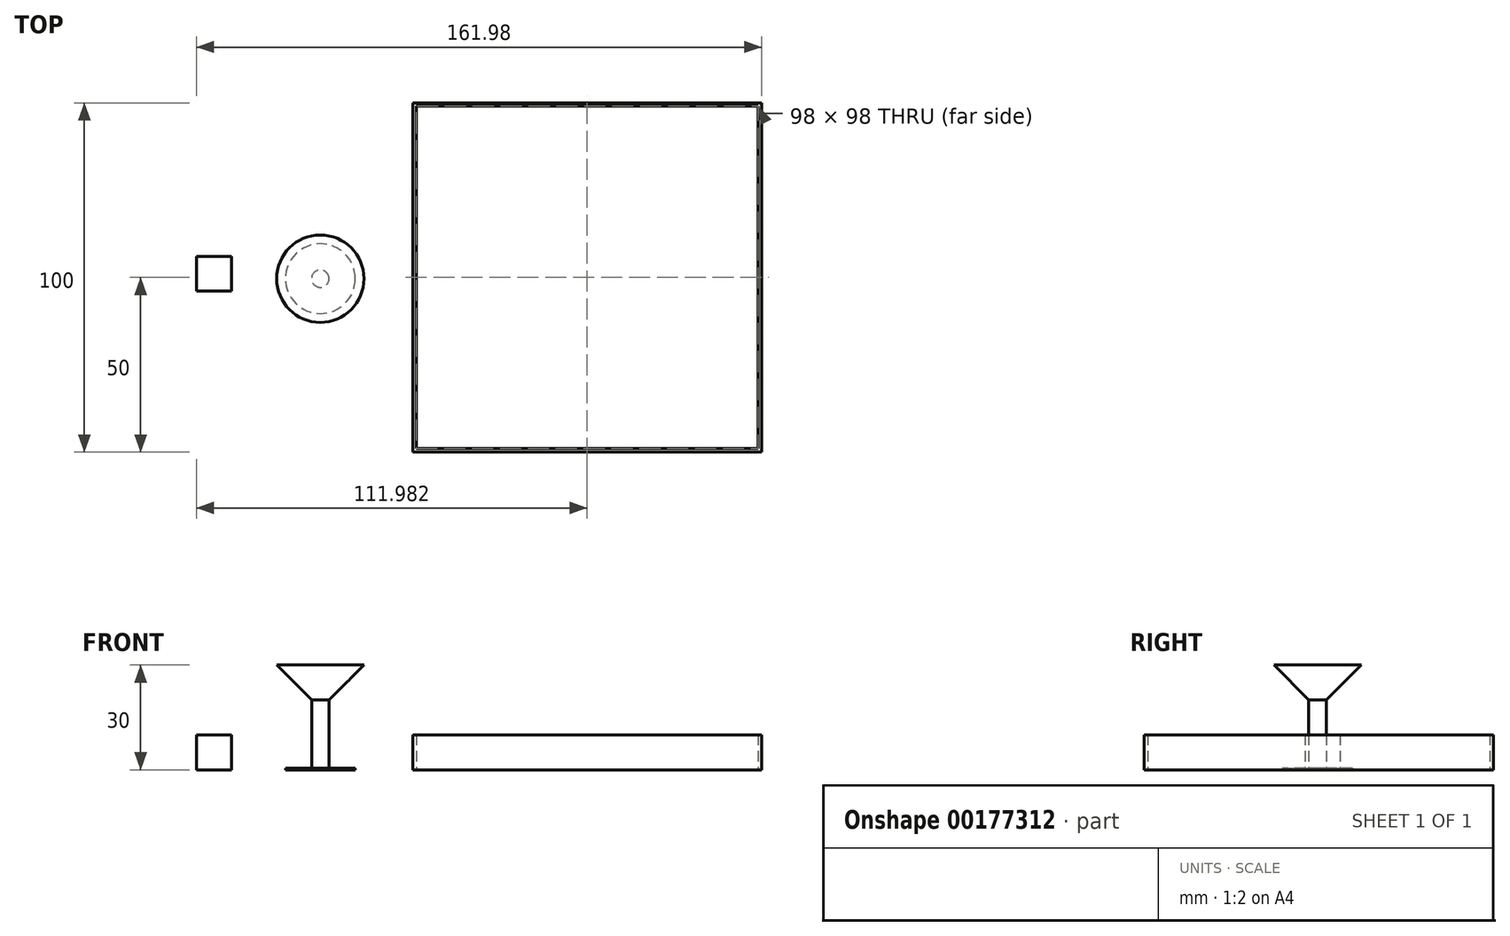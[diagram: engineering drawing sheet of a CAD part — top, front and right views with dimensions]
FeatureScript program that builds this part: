
annotation { "Feature Type Name" : "Feature", "Feature Type Description" : "" }
export const myFeature = defineFeature(function(context is Context, id is Id, definition is map)
    precondition{}
    {
        {
            var Q0;
            Q0=qCreatedBy(makeId("Top.planeOp"),FACE);
            var sketch = newSketch(context, id + "F0", { "sketchPlane" : qUnion([Q0])});
            skCircle(sketch, "E0", {"center": v(0, 0) * mm, "radius": 10 * mm});
            skCircle(sketch, "E1", {"center": v(0, 0) * mm, "radius": 2.5 * mm});
            skSolve(sketch);
        }
        {
            var Q0;
            Q0=makeQuery(id+"F0.imprint","IMPRINT",FACE,{"disambiguationData":[TD([[makeQuery(id+"F0.imprint","IMPRINT",EDGE,{"derivedFrom":sQuery(id+"F0.wireOp",EDGE,"E0")}),1.0]])]});
            extrude(context, id + "F1", {"entities" : qUnion([Q0]), "depth" : 0.4 * mm});
        }
        {
            var Q0;
            Q0=makeQuery(id+"F0.imprint","IMPRINT",FACE,{"disambiguationData":[TD([[makeQuery(id+"F0.imprint","IMPRINT",EDGE,{"derivedFrom":sQuery(id+"F0.wireOp",EDGE,"E1")}),1.0]])]});
            extrude(context, id + "F2", {"entities" : qUnion([Q0]), "operationType" : NewBodyOperationType.ADD, "depth" : 20 * mm});
        }
        {
            var Q0;
            Q0=makeQuery(id+"F2.opExtrude","CAP_FACE",FACE,{"disambiguationData":[OSD([sQuery(id+"F0.wireOp",EDGE,"E1")])],"isStart":false});
            extrude(context, id + "F3", {"entities" : qUnion([Q0]), "operationType" : NewBodyOperationType.ADD, "depth" : 10 * mm, "hasDraft" : true, "draftAngle" : 45 * degree});
        }
        {
            var Q0;
            Q0=qCreatedBy(makeId("Top.planeOp"),FACE);
            var sketch = newSketch(context, id + "F4", { "sketchPlane" : qUnion([Q0])});
            skLineSegment(sketch, "E2.bottom", {"start": v(-35.5, 6.42) * mm, "end": v(-25.5, 6.42) * mm});
            skLineSegment(sketch, "E2.top", {"start": v(-35.5, -3.58) * mm, "end": v(-25.5, -3.58) * mm});
            skLineSegment(sketch, "E2.left", {"start": v(-35.5, 6.42) * mm, "end": v(-35.5, -3.58) * mm});
            skLineSegment(sketch, "E2.right", {"start": v(-25.5, 6.42) * mm, "end": v(-25.5, -3.58) * mm});
            skSolve(sketch);
        }
        {
            var Q0;
            Q0 = qSketchRegion(id + "F4", true);
            extrude(context, id + "F5", {"entities" : qUnion([Q0]), "depth" : 10 * mm});
        }
        {
            var Q0;
            Q0=qCreatedBy(makeId("Top.planeOp"),FACE);
            var sketch = newSketch(context, id + "F6", { "sketchPlane" : qUnion([Q0])});
            skLineSegment(sketch, "E3.bottom", {"start": v(26.48, 50.36) * mm, "end": v(126.48, 50.36) * mm});
            skLineSegment(sketch, "E3.top", {"start": v(26.48, -49.64) * mm, "end": v(126.48, -49.64) * mm});
            skLineSegment(sketch, "E3.left", {"start": v(26.48, 50.36) * mm, "end": v(26.48, -49.64) * mm});
            skLineSegment(sketch, "E3.right", {"start": v(126.48, 50.36) * mm, "end": v(126.48, -49.64) * mm});
            skLineSegment(sketch, "E4.0", {"start": v(27.48, 49.36) * mm, "end": v(125.48, 49.36) * mm});
            skLineSegment(sketch, "E4.1", {"start": v(27.48, 49.36) * mm, "end": v(27.48, -48.64) * mm});
            skLineSegment(sketch, "E4.2", {"start": v(27.48, -48.64) * mm, "end": v(125.48, -48.64) * mm});
            skLineSegment(sketch, "E4.3", {"start": v(125.48, 49.36) * mm, "end": v(125.48, -48.64) * mm});
            skSolve(sketch);
        }
        {
            var Q0;
            Q0=makeQuery(id+"F6.imprint","IMPRINT",FACE,{"disambiguationData":[TD([[makeQuery(id+"F6.imprint","IMPRINT",EDGE,{"derivedFrom":sQuery(id+"F6.wireOp",EDGE,"E3.bottom")}),-1.0]])]});
            extrude(context, id + "F7", {"entities" : qUnion([Q0]), "depth" : 10 * mm});
        }
    });
